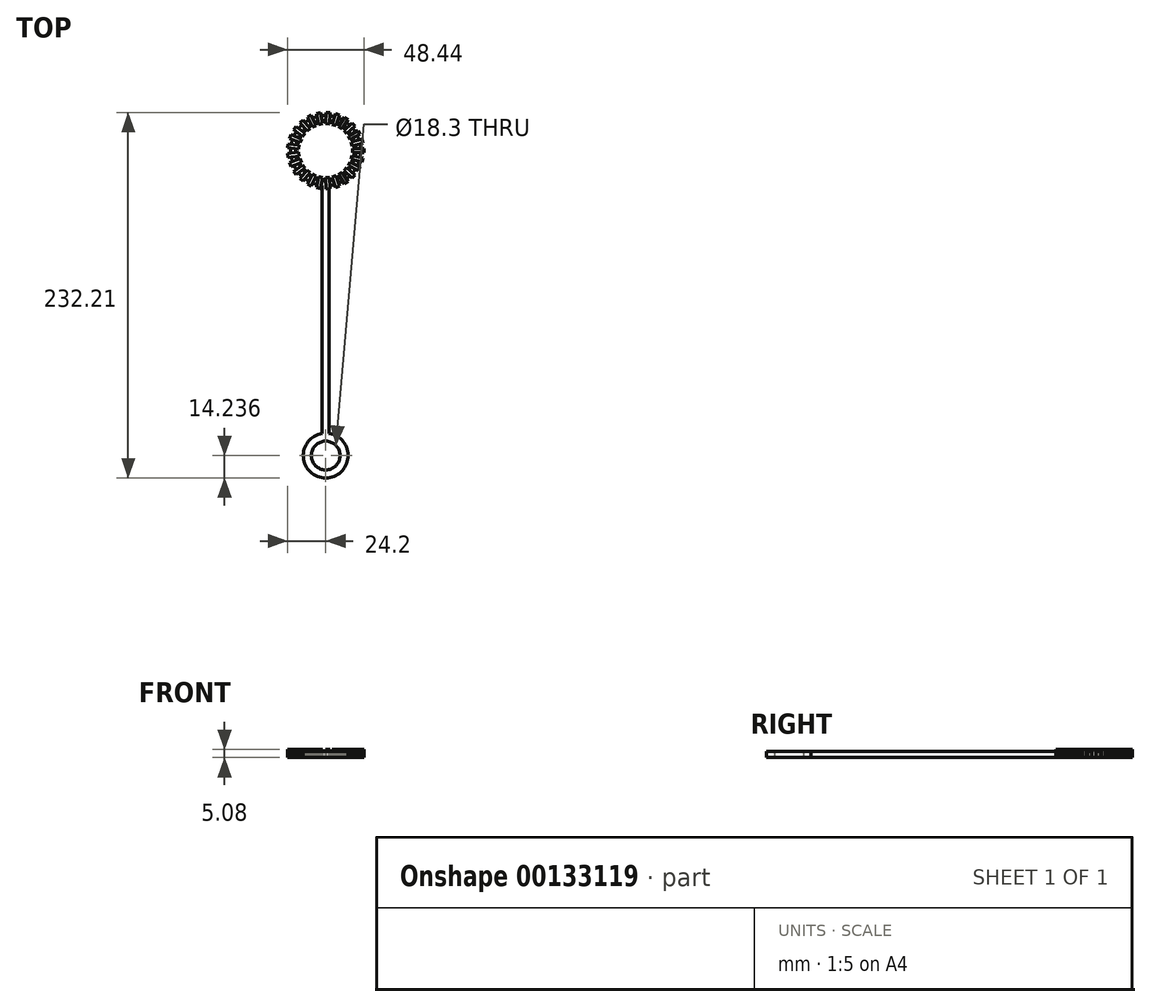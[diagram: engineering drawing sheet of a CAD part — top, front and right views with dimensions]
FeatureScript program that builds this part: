
annotation { "Feature Type Name" : "Feature", "Feature Type Description" : "" }
export const myFeature = defineFeature(function(context is Context, id is Id, definition is map)
    precondition{}
    {
        {
            var Q0;
            Q0=qCreatedBy(makeId("Top.planeOp"),FACE);
            var sketch = newSketch(context, id + "F0", { "sketchPlane" : qUnion([Q0])});
            skCircle(sketch, "E0", {"center": v(0, 0) * mm, "radius": 19.05 * mm});
            skCircle(sketch, "E1", {"center": v(0, 0) * mm, "radius": 22.23 * mm});
            skLineSegment(sketch, "E2", {"start": v(19, 1.27) * mm, "end": v(17.11, 1.27) * mm});
            skLineSegment(sketch, "E3", {"start": v(17.11, 1.27) * mm, "end": v(17.11, 0) * mm});
            skLineSegment(sketch, "E4.MirrorCS", {"start": v(19, -1.27) * mm, "end": v(17.11, -1.27) * mm});
            skLineSegment(sketch, "E5.MirrorCS", {"start": v(17.11, -1.27) * mm, "end": v(17.11, 0) * mm});
            skLineSegment(sketch, "E6.1.0", {"start": v(18.1, 5.96) * mm, "end": v(16.26, 5.49) * mm});
            skLineSegment(sketch, "E6.1.1", {"start": v(18.73, 3.5) * mm, "end": v(16.9, 3.03) * mm});
            skLineSegment(sketch, "E6.1.2", {"start": v(16.9, 3.03) * mm, "end": v(16.58, 4.26) * mm});
            skLineSegment(sketch, "E6.1.3", {"start": v(16.26, 5.49) * mm, "end": v(16.58, 4.26) * mm});
            skLineSegment(sketch, "E6.2.0", {"start": v(16.04, 10.27) * mm, "end": v(14.39, 9.36) * mm});
            skLineSegment(sketch, "E6.2.1", {"start": v(17.27, 8.04) * mm, "end": v(15.6, 7.13) * mm});
            skLineSegment(sketch, "E6.2.2", {"start": v(15.6, 7.13) * mm, "end": v(15, 8.24) * mm});
            skLineSegment(sketch, "E6.2.3", {"start": v(14.39, 9.36) * mm, "end": v(15, 8.24) * mm});
            skLineSegment(sketch, "E6.3.0", {"start": v(12.99, 13.94) * mm, "end": v(11.6, 12.64) * mm});
            skLineSegment(sketch, "E6.3.1", {"start": v(14.73, 12.09) * mm, "end": v(13.35, 10.79) * mm});
            skLineSegment(sketch, "E6.3.2", {"start": v(13.35, 10.79) * mm, "end": v(12.48, 11.72) * mm});
            skLineSegment(sketch, "E6.3.3", {"start": v(11.6, 12.64) * mm, "end": v(12.48, 11.72) * mm});
            skLineSegment(sketch, "E6.4.0", {"start": v(9.11, 16.73) * mm, "end": v(8.1, 15.13) * mm});
            skLineSegment(sketch, "E6.4.1", {"start": v(11.26, 15.37) * mm, "end": v(10.24, 13.77) * mm});
            skLineSegment(sketch, "E6.4.2", {"start": v(10.24, 13.77) * mm, "end": v(9.17, 14.45) * mm});
            skLineSegment(sketch, "E6.4.3", {"start": v(8.1, 15.13) * mm, "end": v(9.17, 14.45) * mm});
            skLineSegment(sketch, "E6.5.0", {"start": v(4.67, 18.47) * mm, "end": v(4.08, 16.67) * mm});
            skLineSegment(sketch, "E6.5.1", {"start": v(7.08, 17.68) * mm, "end": v(6.5, 15.88) * mm});
            skLineSegment(sketch, "E6.5.2", {"start": v(6.5, 15.88) * mm, "end": v(5.29, 16.28) * mm});
            skLineSegment(sketch, "E6.5.3", {"start": v(4.08, 16.67) * mm, "end": v(5.29, 16.28) * mm});
            skLineSegment(sketch, "E6.6.0", {"start": v(-0.07, 19.05) * mm, "end": v(-0.2, 17.16) * mm});
            skLineSegment(sketch, "E6.6.1", {"start": v(2.46, 18.9) * mm, "end": v(2.34, 17) * mm});
            skLineSegment(sketch, "E6.6.2", {"start": v(2.34, 17) * mm, "end": v(1.07, 17.08) * mm});
            skLineSegment(sketch, "E6.6.3", {"start": v(-0.2, 17.16) * mm, "end": v(1.07, 17.08) * mm});
            skLineSegment(sketch, "E6.7.0", {"start": v(-4.8, 18.43) * mm, "end": v(-4.45, 16.57) * mm});
            skLineSegment(sketch, "E6.7.1", {"start": v(-2.31, 18.9) * mm, "end": v(-1.96, 17.05) * mm});
            skLineSegment(sketch, "E6.7.2", {"start": v(-1.96, 17.05) * mm, "end": v(-3.2, 16.81) * mm});
            skLineSegment(sketch, "E6.7.3", {"start": v(-4.45, 16.57) * mm, "end": v(-3.2, 16.81) * mm});
            skLineSegment(sketch, "E6.8.0", {"start": v(-9.24, 16.66) * mm, "end": v(-8.44, 14.94) * mm});
            skLineSegment(sketch, "E6.8.1", {"start": v(-6.94, 17.74) * mm, "end": v(-6.14, 16.03) * mm});
            skLineSegment(sketch, "E6.8.2", {"start": v(-6.14, 16.03) * mm, "end": v(-7.29, 15.49) * mm});
            skLineSegment(sketch, "E6.8.3", {"start": v(-8.44, 14.94) * mm, "end": v(-7.29, 15.49) * mm});
            skLineSegment(sketch, "E6.9.0", {"start": v(-13.1, 13.84) * mm, "end": v(-11.89, 12.38) * mm});
            skLineSegment(sketch, "E6.9.1", {"start": v(-11.14, 15.46) * mm, "end": v(-9.93, 14) * mm});
            skLineSegment(sketch, "E6.9.2", {"start": v(-9.93, 14) * mm, "end": v(-10.9, 13.19) * mm});
            skLineSegment(sketch, "E6.9.3", {"start": v(-11.89, 12.38) * mm, "end": v(-10.9, 13.19) * mm});
            skLineSegment(sketch, "E6.10.0", {"start": v(-16.12, 10.14) * mm, "end": v(-14.6, 9.03) * mm});
            skLineSegment(sketch, "E6.10.1", {"start": v(-14.63, 12.2) * mm, "end": v(-13.1, 11.09) * mm});
            skLineSegment(sketch, "E6.10.2", {"start": v(-13.1, 11.09) * mm, "end": v(-13.85, 10.06) * mm});
            skLineSegment(sketch, "E6.10.3", {"start": v(-14.6, 9.03) * mm, "end": v(-13.85, 10.06) * mm});
            skLineSegment(sketch, "E6.11.0", {"start": v(-18.14, 5.82) * mm, "end": v(-16.38, 5.12) * mm});
            skLineSegment(sketch, "E6.11.1", {"start": v(-17.2, 8.18) * mm, "end": v(-15.45, 7.48) * mm});
            skLineSegment(sketch, "E6.11.2", {"start": v(-15.45, 7.48) * mm, "end": v(-15.91, 6.3) * mm});
            skLineSegment(sketch, "E6.11.3", {"start": v(-16.38, 5.12) * mm, "end": v(-15.91, 6.3) * mm});
            skLineSegment(sketch, "E6.12.0", {"start": v(-19.02, 1.12) * mm, "end": v(-17.14, 0.89) * mm});
            skLineSegment(sketch, "E6.12.1", {"start": v(-18.7, 3.64) * mm, "end": v(-16.82, 3.4) * mm});
            skLineSegment(sketch, "E6.12.2", {"start": v(-16.82, 3.4) * mm, "end": v(-16.98, 2.15) * mm});
            skLineSegment(sketch, "E6.12.3", {"start": v(-17.14, 0.89) * mm, "end": v(-16.98, 2.15) * mm});
            skLineSegment(sketch, "E6.13.0", {"start": v(-18.7, -3.64) * mm, "end": v(-16.82, -3.4) * mm});
            skLineSegment(sketch, "E6.13.1", {"start": v(-19.02, -1.12) * mm, "end": v(-17.14, -0.89) * mm});
            skLineSegment(sketch, "E6.13.2", {"start": v(-17.14, -0.89) * mm, "end": v(-16.98, -2.15) * mm});
            skLineSegment(sketch, "E6.13.3", {"start": v(-16.82, -3.4) * mm, "end": v(-16.98, -2.15) * mm});
            skLineSegment(sketch, "E6.14.0", {"start": v(-17.2, -8.18) * mm, "end": v(-15.45, -7.48) * mm});
            skLineSegment(sketch, "E6.14.1", {"start": v(-18.14, -5.82) * mm, "end": v(-16.38, -5.12) * mm});
            skLineSegment(sketch, "E6.14.2", {"start": v(-16.38, -5.12) * mm, "end": v(-15.91, -6.3) * mm});
            skLineSegment(sketch, "E6.14.3", {"start": v(-15.45, -7.48) * mm, "end": v(-15.91, -6.3) * mm});
            skLineSegment(sketch, "E7.2.15.0", {"start": v(-14.63, -12.2) * mm, "end": v(-13.1, -11.09) * mm});
            skLineSegment(sketch, "E7.3.15.0", {"start": v(-16.12, -10.14) * mm, "end": v(-14.6, -9.03) * mm});
            skLineSegment(sketch, "E7.6.15.0", {"start": v(-14.6, -9.03) * mm, "end": v(-13.85, -10.06) * mm});
            skLineSegment(sketch, "E7.9.15.0", {"start": v(-13.1, -11.09) * mm, "end": v(-13.85, -10.06) * mm});
            skLineSegment(sketch, "E7.2.16.0", {"start": v(-11.14, -15.46) * mm, "end": v(-9.93, -14) * mm});
            skLineSegment(sketch, "E7.3.16.0", {"start": v(-13.1, -13.84) * mm, "end": v(-11.89, -12.38) * mm});
            skLineSegment(sketch, "E7.6.16.0", {"start": v(-11.89, -12.38) * mm, "end": v(-10.9, -13.19) * mm});
            skLineSegment(sketch, "E7.9.16.0", {"start": v(-9.93, -14) * mm, "end": v(-10.9, -13.19) * mm});
            skLineSegment(sketch, "E7.2.17.0", {"start": v(-6.94, -17.74) * mm, "end": v(-6.14, -16.03) * mm});
            skLineSegment(sketch, "E7.3.17.0", {"start": v(-9.24, -16.66) * mm, "end": v(-8.44, -14.94) * mm});
            skLineSegment(sketch, "E7.6.17.0", {"start": v(-8.44, -14.94) * mm, "end": v(-7.29, -15.49) * mm});
            skLineSegment(sketch, "E7.9.17.0", {"start": v(-6.14, -16.03) * mm, "end": v(-7.29, -15.49) * mm});
            skLineSegment(sketch, "E7.2.18.0", {"start": v(-2.31, -18.9) * mm, "end": v(-1.96, -17.05) * mm});
            skLineSegment(sketch, "E7.3.18.0", {"start": v(-4.8, -18.43) * mm, "end": v(-4.45, -16.57) * mm});
            skLineSegment(sketch, "E7.6.18.0", {"start": v(-4.45, -16.57) * mm, "end": v(-3.2, -16.81) * mm});
            skLineSegment(sketch, "E7.9.18.0", {"start": v(-1.96, -17.05) * mm, "end": v(-3.2, -16.81) * mm});
            skLineSegment(sketch, "E7.2.19.0", {"start": v(2.46, -18.9) * mm, "end": v(2.34, -17) * mm});
            skLineSegment(sketch, "E7.3.19.0", {"start": v(-0.07, -19.05) * mm, "end": v(-0.2, -17.16) * mm});
            skLineSegment(sketch, "E7.6.19.0", {"start": v(-0.2, -17.16) * mm, "end": v(1.07, -17.08) * mm});
            skLineSegment(sketch, "E7.9.19.0", {"start": v(2.34, -17) * mm, "end": v(1.07, -17.08) * mm});
            skLineSegment(sketch, "E8.2.20.0", {"start": v(7.08, -17.68) * mm, "end": v(6.5, -15.88) * mm});
            skLineSegment(sketch, "E8.3.20.0", {"start": v(4.67, -18.47) * mm, "end": v(4.08, -16.67) * mm});
            skLineSegment(sketch, "E8.6.20.0", {"start": v(4.08, -16.67) * mm, "end": v(5.29, -16.28) * mm});
            skLineSegment(sketch, "E8.9.20.0", {"start": v(6.5, -15.88) * mm, "end": v(5.29, -16.28) * mm});
            skLineSegment(sketch, "E8.2.21.0", {"start": v(11.26, -15.37) * mm, "end": v(10.24, -13.77) * mm});
            skLineSegment(sketch, "E8.3.21.0", {"start": v(9.11, -16.73) * mm, "end": v(8.1, -15.13) * mm});
            skLineSegment(sketch, "E8.6.21.0", {"start": v(8.1, -15.13) * mm, "end": v(9.17, -14.45) * mm});
            skLineSegment(sketch, "E8.9.21.0", {"start": v(10.24, -13.77) * mm, "end": v(9.17, -14.45) * mm});
            skLineSegment(sketch, "E8.2.22.0", {"start": v(14.73, -12.09) * mm, "end": v(13.35, -10.79) * mm});
            skLineSegment(sketch, "E8.3.22.0", {"start": v(12.99, -13.94) * mm, "end": v(11.6, -12.64) * mm});
            skLineSegment(sketch, "E8.6.22.0", {"start": v(11.6, -12.64) * mm, "end": v(12.48, -11.72) * mm});
            skLineSegment(sketch, "E8.9.22.0", {"start": v(13.35, -10.79) * mm, "end": v(12.48, -11.72) * mm});
            skLineSegment(sketch, "E8.2.23.0", {"start": v(17.27, -8.04) * mm, "end": v(15.6, -7.13) * mm});
            skLineSegment(sketch, "E8.3.23.0", {"start": v(16.04, -10.27) * mm, "end": v(14.39, -9.36) * mm});
            skLineSegment(sketch, "E8.6.23.0", {"start": v(14.39, -9.36) * mm, "end": v(15, -8.24) * mm});
            skLineSegment(sketch, "E8.9.23.0", {"start": v(15.6, -7.13) * mm, "end": v(15, -8.24) * mm});
            skLineSegment(sketch, "E8.2.24.0", {"start": v(18.73, -3.5) * mm, "end": v(16.9, -3.03) * mm});
            skLineSegment(sketch, "E8.3.24.0", {"start": v(18.1, -5.96) * mm, "end": v(16.26, -5.49) * mm});
            skLineSegment(sketch, "E8.6.24.0", {"start": v(16.26, -5.49) * mm, "end": v(16.58, -4.26) * mm});
            skLineSegment(sketch, "E8.9.24.0", {"start": v(16.9, -3.03) * mm, "end": v(16.58, -4.26) * mm});
            skSolve(sketch);
        }
        {
            var Q0;
            Q0=makeQuery(id+"F0.imprint","IMPRINT",FACE,{"disambiguationData":[TD([[makeQuery(id+"F0.imprint","IMPRINT",EDGE,{"derivedFrom":sQuery(id+"F0.wireOp",EDGE,"E1")}),1.0]])]});
            var Q1;
            {var subQ1=sQuery(id+"F0.wireOp",EDGE,"E6.5.0");Q1=makeQuery(id+"F0.imprint","IMPRINT",FACE,{"disambiguationData":[TD([[makeQuery(id+"F0.imprint","IMPRINT",EDGE,{"derivedFrom":subQ1}),1.0]])]});}
            var Q2;
            {var subQ1=sQuery(id+"F0.wireOp",EDGE,"E6.6.0");Q2=makeQuery(id+"F0.imprint","IMPRINT",FACE,{"disambiguationData":[TD([[makeQuery(id+"F0.imprint","IMPRINT",EDGE,{"derivedFrom":subQ1}),1.0]])]});}
            var Q3;
            {var subQ1=sQuery(id+"F0.wireOp",EDGE,"E6.7.0");Q3=makeQuery(id+"F0.imprint","IMPRINT",FACE,{"disambiguationData":[TD([[makeQuery(id+"F0.imprint","IMPRINT",EDGE,{"derivedFrom":subQ1}),1.0]])]});}
            var Q4;
            {var subQ1=sQuery(id+"F0.wireOp",EDGE,"E6.8.0");Q4=makeQuery(id+"F0.imprint","IMPRINT",FACE,{"disambiguationData":[TD([[makeQuery(id+"F0.imprint","IMPRINT",EDGE,{"derivedFrom":subQ1}),1.0]])]});}
            var Q5;
            {var subQ1=sQuery(id+"F0.wireOp",EDGE,"E6.10.0");Q5=makeQuery(id+"F0.imprint","IMPRINT",FACE,{"disambiguationData":[TD([[makeQuery(id+"F0.imprint","IMPRINT",EDGE,{"derivedFrom":subQ1}),1.0]])]});}
            var Q6;
            {var subQ1=sQuery(id+"F0.wireOp",EDGE,"E6.11.0");Q6=makeQuery(id+"F0.imprint","IMPRINT",FACE,{"disambiguationData":[TD([[makeQuery(id+"F0.imprint","IMPRINT",EDGE,{"derivedFrom":subQ1}),1.0]])]});}
            var Q7;
            {var subQ1=sQuery(id+"F0.wireOp",EDGE,"E6.9.0");Q7=makeQuery(id+"F0.imprint","IMPRINT",FACE,{"disambiguationData":[TD([[makeQuery(id+"F0.imprint","IMPRINT",EDGE,{"derivedFrom":subQ1}),1.0]])]});}
            var Q8;
            {var subQ1=sQuery(id+"F0.wireOp",EDGE,"E6.4.0");Q8=makeQuery(id+"F0.imprint","IMPRINT",FACE,{"disambiguationData":[TD([[makeQuery(id+"F0.imprint","IMPRINT",EDGE,{"derivedFrom":subQ1}),1.0]])]});}
            var Q9;
            {var subQ1=sQuery(id+"F0.wireOp",EDGE,"E6.3.0");Q9=makeQuery(id+"F0.imprint","IMPRINT",FACE,{"disambiguationData":[TD([[makeQuery(id+"F0.imprint","IMPRINT",EDGE,{"derivedFrom":subQ1}),1.0]])]});}
            var Q10;
            {var subQ1=sQuery(id+"F0.wireOp",EDGE,"E6.2.0");Q10=makeQuery(id+"F0.imprint","IMPRINT",FACE,{"disambiguationData":[TD([[makeQuery(id+"F0.imprint","IMPRINT",EDGE,{"derivedFrom":subQ1}),1.0]])]});}
            var Q11;
            {var subQ1=sQuery(id+"F0.wireOp",EDGE,"E6.1.0");Q11=makeQuery(id+"F0.imprint","IMPRINT",FACE,{"disambiguationData":[TD([[makeQuery(id+"F0.imprint","IMPRINT",EDGE,{"derivedFrom":subQ1}),1.0]])]});}
            var Q12;
            {var subQ1=sQuery(id+"F0.wireOp",EDGE,"E2");Q12=makeQuery(id+"F0.imprint","IMPRINT",FACE,{"disambiguationData":[TD([[makeQuery(id+"F0.imprint","IMPRINT",EDGE,{"derivedFrom":subQ1}),1.0]])]});}
            var Q13;
            {var subQ1=sQuery(id+"F0.wireOp",EDGE,"E7.2.19.0");Q13=makeQuery(id+"F0.imprint","IMPRINT",FACE,{"disambiguationData":[TD([[makeQuery(id+"F0.imprint","IMPRINT",EDGE,{"derivedFrom":subQ1}),1.0]])]});}
            var Q14;
            {var subQ1=sQuery(id+"F0.wireOp",EDGE,"E7.2.18.0");Q14=makeQuery(id+"F0.imprint","IMPRINT",FACE,{"disambiguationData":[TD([[makeQuery(id+"F0.imprint","IMPRINT",EDGE,{"derivedFrom":subQ1}),1.0]])]});}
            var Q15;
            {var subQ1=sQuery(id+"F0.wireOp",EDGE,"E7.2.17.0");Q15=makeQuery(id+"F0.imprint","IMPRINT",FACE,{"disambiguationData":[TD([[makeQuery(id+"F0.imprint","IMPRINT",EDGE,{"derivedFrom":subQ1}),1.0]])]});}
            var Q16;
            {var subQ0=sQuery(id+"F0.wireOp",EDGE,"E7.2.16.0");Q16=makeQuery(id+"F0.imprint","IMPRINT",FACE,{"disambiguationData":[TD([[makeQuery(id+"F0.imprint","IMPRINT",EDGE,{"derivedFrom":subQ0}),1.0]])]});}
            var Q17;
            {var subQ1=sQuery(id+"F0.wireOp",EDGE,"E7.2.15.0");Q17=makeQuery(id+"F0.imprint","IMPRINT",FACE,{"disambiguationData":[TD([[makeQuery(id+"F0.imprint","IMPRINT",EDGE,{"derivedFrom":subQ1}),1.0]])]});}
            var Q18;
            {var subQ1=sQuery(id+"F0.wireOp",EDGE,"E6.14.0");Q18=makeQuery(id+"F0.imprint","IMPRINT",FACE,{"disambiguationData":[TD([[makeQuery(id+"F0.imprint","IMPRINT",EDGE,{"derivedFrom":subQ1}),1.0]])]});}
            var Q19;
            {var subQ1=sQuery(id+"F0.wireOp",EDGE,"E6.13.0");Q19=makeQuery(id+"F0.imprint","IMPRINT",FACE,{"disambiguationData":[TD([[makeQuery(id+"F0.imprint","IMPRINT",EDGE,{"derivedFrom":subQ1}),1.0]])]});}
            var Q20;
            {var subQ1=sQuery(id+"F0.wireOp",EDGE,"E6.12.0");Q20=makeQuery(id+"F0.imprint","IMPRINT",FACE,{"disambiguationData":[TD([[makeQuery(id+"F0.imprint","IMPRINT",EDGE,{"derivedFrom":subQ1}),1.0]])]});}
            extrude(context, id + "F1", {"entities" : qUnion([Q0, Q1, Q2, Q3, Q4, Q5, Q6, Q7, Q8, Q9, Q10, Q11, Q12, Q13, Q14, Q15, Q16, Q17, Q18, Q19, Q20]), "depth" : 3.8 * mm});
        }
        {
            var Q0;
            Q0=makeQuery(id+"F1.opExtrude","CAP_FACE",FACE,{"disambiguationData":[OSD([sQuery(id+"F0.wireOp",EDGE,"E0"),sQuery(id+"F0.wireOp",EDGE,"E1"),sQuery(id+"F0.wireOp",EDGE,"E2"),sQuery(id+"F0.wireOp",EDGE,"E3"),sQuery(id+"F0.wireOp",EDGE,"E4.MirrorCS"),sQuery(id+"F0.wireOp",EDGE,"E5.MirrorCS"),sQuery(id+"F0.wireOp",EDGE,"E6.1.0"),sQuery(id+"F0.wireOp",EDGE,"E6.1.1"),sQuery(id+"F0.wireOp",EDGE,"E6.1.2"),sQuery(id+"F0.wireOp",EDGE,"E6.1.3"),sQuery(id+"F0.wireOp",EDGE,"E6.2.0"),sQuery(id+"F0.wireOp",EDGE,"E6.2.1"),sQuery(id+"F0.wireOp",EDGE,"E6.2.2"),sQuery(id+"F0.wireOp",EDGE,"E6.2.3"),sQuery(id+"F0.wireOp",EDGE,"E6.3.0"),sQuery(id+"F0.wireOp",EDGE,"E6.3.1"),sQuery(id+"F0.wireOp",EDGE,"E6.3.2"),sQuery(id+"F0.wireOp",EDGE,"E6.3.3"),sQuery(id+"F0.wireOp",EDGE,"E6.4.0"),sQuery(id+"F0.wireOp",EDGE,"E6.4.1"),sQuery(id+"F0.wireOp",EDGE,"E6.4.2"),sQuery(id+"F0.wireOp",EDGE,"E6.4.3"),sQuery(id+"F0.wireOp",EDGE,"E6.5.0"),sQuery(id+"F0.wireOp",EDGE,"E6.5.1"),sQuery(id+"F0.wireOp",EDGE,"E6.5.2"),sQuery(id+"F0.wireOp",EDGE,"E6.5.3"),sQuery(id+"F0.wireOp",EDGE,"E6.6.0"),sQuery(id+"F0.wireOp",EDGE,"E6.6.1"),sQuery(id+"F0.wireOp",EDGE,"E6.6.2"),sQuery(id+"F0.wireOp",EDGE,"E6.6.3"),sQuery(id+"F0.wireOp",EDGE,"E6.7.0"),sQuery(id+"F0.wireOp",EDGE,"E6.7.1"),sQuery(id+"F0.wireOp",EDGE,"E6.7.2"),sQuery(id+"F0.wireOp",EDGE,"E6.7.3"),sQuery(id+"F0.wireOp",EDGE,"E6.8.0"),sQuery(id+"F0.wireOp",EDGE,"E6.8.1"),sQuery(id+"F0.wireOp",EDGE,"E6.8.2"),sQuery(id+"F0.wireOp",EDGE,"E6.8.3"),sQuery(id+"F0.wireOp",EDGE,"E6.9.0"),sQuery(id+"F0.wireOp",EDGE,"E6.9.1"),sQuery(id+"F0.wireOp",EDGE,"E6.9.2"),sQuery(id+"F0.wireOp",EDGE,"E6.9.3"),sQuery(id+"F0.wireOp",EDGE,"E6.10.0"),sQuery(id+"F0.wireOp",EDGE,"E6.10.1"),sQuery(id+"F0.wireOp",EDGE,"E6.10.2"),sQuery(id+"F0.wireOp",EDGE,"E6.10.3"),sQuery(id+"F0.wireOp",EDGE,"E6.11.0"),sQuery(id+"F0.wireOp",EDGE,"E6.11.1"),sQuery(id+"F0.wireOp",EDGE,"E6.11.2"),sQuery(id+"F0.wireOp",EDGE,"E6.11.3"),sQuery(id+"F0.wireOp",EDGE,"E6.12.0"),sQuery(id+"F0.wireOp",EDGE,"E6.12.1"),sQuery(id+"F0.wireOp",EDGE,"E6.12.2"),sQuery(id+"F0.wireOp",EDGE,"E6.12.3"),sQuery(id+"F0.wireOp",EDGE,"E6.13.0"),sQuery(id+"F0.wireOp",EDGE,"E6.13.1"),sQuery(id+"F0.wireOp",EDGE,"E6.13.2"),sQuery(id+"F0.wireOp",EDGE,"E6.13.3"),sQuery(id+"F0.wireOp",EDGE,"E6.14.0"),sQuery(id+"F0.wireOp",EDGE,"E6.14.1"),sQuery(id+"F0.wireOp",EDGE,"E6.14.2"),sQuery(id+"F0.wireOp",EDGE,"E6.14.3"),sQuery(id+"F0.wireOp",EDGE,"E7.2.15.0"),sQuery(id+"F0.wireOp",EDGE,"E7.3.15.0"),sQuery(id+"F0.wireOp",EDGE,"E7.6.15.0"),sQuery(id+"F0.wireOp",EDGE,"E7.9.15.0"),sQuery(id+"F0.wireOp",EDGE,"E7.2.16.0"),sQuery(id+"F0.wireOp",EDGE,"E7.3.16.0"),sQuery(id+"F0.wireOp",EDGE,"E7.6.16.0"),sQuery(id+"F0.wireOp",EDGE,"E7.9.16.0"),sQuery(id+"F0.wireOp",EDGE,"E7.2.17.0"),sQuery(id+"F0.wireOp",EDGE,"E7.3.17.0"),sQuery(id+"F0.wireOp",EDGE,"E7.6.17.0"),sQuery(id+"F0.wireOp",EDGE,"E7.9.17.0"),sQuery(id+"F0.wireOp",EDGE,"E7.2.18.0"),sQuery(id+"F0.wireOp",EDGE,"E7.3.18.0"),sQuery(id+"F0.wireOp",EDGE,"E7.6.18.0"),sQuery(id+"F0.wireOp",EDGE,"E7.9.18.0"),sQuery(id+"F0.wireOp",EDGE,"E7.2.19.0"),sQuery(id+"F0.wireOp",EDGE,"E7.3.19.0"),sQuery(id+"F0.wireOp",EDGE,"E7.6.19.0"),sQuery(id+"F0.wireOp",EDGE,"E7.9.19.0")])],"isStart":false});
            var sketch = newSketch(context, id + "F2", { "sketchPlane" : qUnion([Q0])});
            skLineSegment(sketch, "E9.bottom", {"start": v(17.11, 1.27) * mm, "end": v(22.19, 1.27) * mm});
            skLineSegment(sketch, "E9.top", {"start": v(17.11, -1.27) * mm, "end": v(22.19, -1.27) * mm});
            skLineSegment(sketch, "E9.left", {"start": v(17.11, 1.27) * mm, "end": v(17.11, -1.27) * mm});
            skLineSegment(sketch, "E10.1.0", {"start": v(16.26, 5.49) * mm, "end": v(21.18, 6.75) * mm});
            skLineSegment(sketch, "E10.1.1", {"start": v(16.26, 5.49) * mm, "end": v(16.9, 3.03) * mm});
            skLineSegment(sketch, "E10.1.2", {"start": v(16.9, 3.03) * mm, "end": v(21.8, 4.3) * mm});
            skLineSegment(sketch, "E10.1.3", {"start": v(21.18, 6.75) * mm, "end": v(21.8, 4.3) * mm});
            skLineSegment(sketch, "E10.2.0", {"start": v(14.39, 9.36) * mm, "end": v(18.83, 11.8) * mm});
            skLineSegment(sketch, "E10.2.1", {"start": v(14.39, 9.36) * mm, "end": v(15.6, 7.13) * mm});
            skLineSegment(sketch, "E10.2.2", {"start": v(15.6, 7.13) * mm, "end": v(20.05, 9.58) * mm});
            skLineSegment(sketch, "E10.2.3", {"start": v(18.83, 11.8) * mm, "end": v(20.05, 9.58) * mm});
            skLineSegment(sketch, "E10.3.0", {"start": v(11.6, 12.64) * mm, "end": v(15.3, 16.12) * mm});
            skLineSegment(sketch, "E10.3.1", {"start": v(11.6, 12.64) * mm, "end": v(13.34, 10.8) * mm});
            skLineSegment(sketch, "E10.3.2", {"start": v(13.34, 10.8) * mm, "end": v(17.04, 14.27) * mm});
            skLineSegment(sketch, "E10.3.3", {"start": v(15.3, 16.12) * mm, "end": v(17.04, 14.27) * mm});
            skLineSegment(sketch, "E10.4.0", {"start": v(8.1, 15.13) * mm, "end": v(10.82, 19.42) * mm});
            skLineSegment(sketch, "E10.4.1", {"start": v(8.1, 15.13) * mm, "end": v(10.24, 13.77) * mm});
            skLineSegment(sketch, "E10.4.2", {"start": v(10.24, 13.77) * mm, "end": v(12.96, 18.06) * mm});
            skLineSegment(sketch, "E10.4.3", {"start": v(10.82, 19.42) * mm, "end": v(12.96, 18.06) * mm});
            skLineSegment(sketch, "E10.5.0", {"start": v(4.08, 16.67) * mm, "end": v(5.65, 21.5) * mm});
            skLineSegment(sketch, "E10.5.1", {"start": v(4.08, 16.67) * mm, "end": v(6.5, 15.89) * mm});
            skLineSegment(sketch, "E10.5.2", {"start": v(6.5, 15.89) * mm, "end": v(8.06, 20.71) * mm});
            skLineSegment(sketch, "E10.5.3", {"start": v(5.65, 21.5) * mm, "end": v(8.06, 20.71) * mm});
            skLineSegment(sketch, "E10.6.0", {"start": v(-0.2, 17.16) * mm, "end": v(0.13, 22.22) * mm});
            skLineSegment(sketch, "E10.6.1", {"start": v(-0.2, 17.16) * mm, "end": v(2.34, 17) * mm});
            skLineSegment(sketch, "E10.6.2", {"start": v(2.34, 17) * mm, "end": v(2.66, 22.07) * mm});
            skLineSegment(sketch, "E10.6.3", {"start": v(0.13, 22.22) * mm, "end": v(2.66, 22.07) * mm});
            skLineSegment(sketch, "E10.7.0", {"start": v(-4.45, 16.57) * mm, "end": v(-5.4, 21.56) * mm});
            skLineSegment(sketch, "E10.7.1", {"start": v(-4.45, 16.57) * mm, "end": v(-1.96, 17.05) * mm});
            skLineSegment(sketch, "E10.7.2", {"start": v(-1.96, 17.05) * mm, "end": v(-2.91, 22.03) * mm});
            skLineSegment(sketch, "E10.7.3", {"start": v(-5.4, 21.56) * mm, "end": v(-2.91, 22.03) * mm});
            skLineSegment(sketch, "E10.8.0", {"start": v(-8.44, 14.94) * mm, "end": v(-10.6, 19.54) * mm});
            skLineSegment(sketch, "E10.8.1", {"start": v(-8.44, 14.94) * mm, "end": v(-6.14, 16.03) * mm});
            skLineSegment(sketch, "E10.8.2", {"start": v(-6.14, 16.03) * mm, "end": v(-8.3, 20.62) * mm});
            skLineSegment(sketch, "E10.8.3", {"start": v(-10.6, 19.54) * mm, "end": v(-8.3, 20.62) * mm});
            skLineSegment(sketch, "E10.9.0", {"start": v(-11.89, 12.38) * mm, "end": v(-15.12, 16.29) * mm});
            skLineSegment(sketch, "E10.9.1", {"start": v(-11.89, 12.38) * mm, "end": v(-9.93, 14) * mm});
            skLineSegment(sketch, "E10.9.2", {"start": v(-9.93, 14) * mm, "end": v(-13.17, 17.9) * mm});
            skLineSegment(sketch, "E10.9.3", {"start": v(-15.12, 16.29) * mm, "end": v(-13.17, 17.9) * mm});
            skLineSegment(sketch, "E10.10.0", {"start": v(-14.6, 9.03) * mm, "end": v(-18.7, 12.01) * mm});
            skLineSegment(sketch, "E10.10.1", {"start": v(-14.6, 9.03) * mm, "end": v(-13.1, 11.09) * mm});
            skLineSegment(sketch, "E10.10.2", {"start": v(-13.1, 11.09) * mm, "end": v(-17.2, 14.07) * mm});
            skLineSegment(sketch, "E10.10.3", {"start": v(-18.7, 12.01) * mm, "end": v(-17.2, 14.07) * mm});
            skLineSegment(sketch, "E10.11.0", {"start": v(-16.38, 5.12) * mm, "end": v(-21.1, 6.99) * mm});
            skLineSegment(sketch, "E10.11.1", {"start": v(-16.38, 5.12) * mm, "end": v(-15.45, 7.48) * mm});
            skLineSegment(sketch, "E10.11.2", {"start": v(-15.45, 7.48) * mm, "end": v(-20.16, 9.35) * mm});
            skLineSegment(sketch, "E10.11.3", {"start": v(-21.1, 6.99) * mm, "end": v(-20.16, 9.35) * mm});
            skLineSegment(sketch, "E10.12.0", {"start": v(-17.14, 0.89) * mm, "end": v(-22.17, 1.52) * mm});
            skLineSegment(sketch, "E10.12.1", {"start": v(-17.14, 0.89) * mm, "end": v(-16.82, 3.4) * mm});
            skLineSegment(sketch, "E10.12.2", {"start": v(-16.82, 3.4) * mm, "end": v(-21.85, 4.04) * mm});
            skLineSegment(sketch, "E10.12.3", {"start": v(-22.17, 1.52) * mm, "end": v(-21.85, 4.04) * mm});
            skLineSegment(sketch, "E10.13.0", {"start": v(-16.82, -3.4) * mm, "end": v(-21.85, -4.04) * mm});
            skLineSegment(sketch, "E10.13.1", {"start": v(-16.82, -3.4) * mm, "end": v(-17.14, -0.89) * mm});
            skLineSegment(sketch, "E10.13.2", {"start": v(-17.14, -0.89) * mm, "end": v(-22.17, -1.52) * mm});
            skLineSegment(sketch, "E10.13.3", {"start": v(-21.85, -4.04) * mm, "end": v(-22.17, -1.52) * mm});
            skLineSegment(sketch, "E10.14.0", {"start": v(-15.45, -7.48) * mm, "end": v(-20.16, -9.35) * mm});
            skLineSegment(sketch, "E10.14.1", {"start": v(-15.45, -7.48) * mm, "end": v(-16.38, -5.12) * mm});
            skLineSegment(sketch, "E10.14.2", {"start": v(-16.38, -5.12) * mm, "end": v(-21.1, -6.99) * mm});
            skLineSegment(sketch, "E10.14.3", {"start": v(-20.16, -9.35) * mm, "end": v(-21.1, -6.99) * mm});
            skLineSegment(sketch, "E10.15.0", {"start": v(-13.1, -11.09) * mm, "end": v(-17.2, -14.07) * mm});
            skLineSegment(sketch, "E10.15.1", {"start": v(-13.1, -11.09) * mm, "end": v(-14.6, -9.03) * mm});
            skLineSegment(sketch, "E10.15.2", {"start": v(-14.6, -9.03) * mm, "end": v(-18.7, -12.02) * mm});
            skLineSegment(sketch, "E10.15.3", {"start": v(-17.2, -14.07) * mm, "end": v(-18.7, -12.02) * mm});
            skLineSegment(sketch, "E10.16.0", {"start": v(-9.93, -14) * mm, "end": v(-13.17, -17.9) * mm});
            skLineSegment(sketch, "E10.16.1", {"start": v(-9.93, -14) * mm, "end": v(-11.89, -12.38) * mm});
            skLineSegment(sketch, "E10.16.2", {"start": v(-11.89, -12.38) * mm, "end": v(-15.12, -16.29) * mm});
            skLineSegment(sketch, "E10.16.3", {"start": v(-13.17, -17.9) * mm, "end": v(-15.12, -16.29) * mm});
            skLineSegment(sketch, "E10.17.0", {"start": v(-6.14, -16.03) * mm, "end": v(-8.3, -20.62) * mm});
            skLineSegment(sketch, "E10.17.1", {"start": v(-6.14, -16.03) * mm, "end": v(-8.43, -14.95) * mm});
            skLineSegment(sketch, "E10.17.2", {"start": v(-8.43, -14.95) * mm, "end": v(-10.6, -19.54) * mm});
            skLineSegment(sketch, "E10.17.3", {"start": v(-8.3, -20.62) * mm, "end": v(-10.6, -19.54) * mm});
            skLineSegment(sketch, "E10.18.0", {"start": v(-1.96, -17.05) * mm, "end": v(-2.91, -22.03) * mm});
            skLineSegment(sketch, "E10.18.1", {"start": v(-1.96, -17.05) * mm, "end": v(-4.45, -16.57) * mm});
            skLineSegment(sketch, "E10.18.2", {"start": v(-4.45, -16.57) * mm, "end": v(-5.4, -21.56) * mm});
            skLineSegment(sketch, "E10.18.3", {"start": v(-2.91, -22.03) * mm, "end": v(-5.4, -21.56) * mm});
            skLineSegment(sketch, "E10.19.0", {"start": v(2.34, -17) * mm, "end": v(2.66, -22.07) * mm});
            skLineSegment(sketch, "E10.19.1", {"start": v(2.34, -17) * mm, "end": v(-0.2, -17.16) * mm});
            skLineSegment(sketch, "E10.19.2", {"start": v(-0.2, -17.16) * mm, "end": v(0.13, -22.22) * mm});
            skLineSegment(sketch, "E10.19.3", {"start": v(2.66, -22.07) * mm, "end": v(0.13, -22.22) * mm});
            skPoint(sketch, "E10.center", {"position": v(0, 0) * mm});
            skLineSegment(sketch, "E11.bottom", {"start": v(22.19, 1.27) * mm, "end": v(24.24, 1.27) * mm});
            skLineSegment(sketch, "E11.top", {"start": v(22.19, -1.27) * mm, "end": v(24.24, -1.27) * mm});
            skLineSegment(sketch, "E11.right", {"start": v(24.24, 1.27) * mm, "end": v(24.24, -1.27) * mm});
            skLineSegment(sketch, "E12.1.0", {"start": v(21.8, 4.3) * mm, "end": v(23.79, 4.8) * mm});
            skLineSegment(sketch, "E12.1.1", {"start": v(23.16, 7.26) * mm, "end": v(23.79, 4.8) * mm});
            skLineSegment(sketch, "E12.1.2", {"start": v(21.18, 6.75) * mm, "end": v(23.16, 7.26) * mm});
            skLineSegment(sketch, "E12.2.0", {"start": v(20.05, 9.58) * mm, "end": v(21.85, 10.56) * mm});
            skLineSegment(sketch, "E12.2.1", {"start": v(20.63, 12.79) * mm, "end": v(21.85, 10.56) * mm});
            skLineSegment(sketch, "E12.2.2", {"start": v(18.83, 11.8) * mm, "end": v(20.63, 12.79) * mm});
            skLineSegment(sketch, "E12.3.0", {"start": v(17.04, 14.27) * mm, "end": v(18.53, 15.67) * mm});
            skLineSegment(sketch, "E12.3.1", {"start": v(16.8, 17.52) * mm, "end": v(18.53, 15.67) * mm});
            skLineSegment(sketch, "E12.3.2", {"start": v(15.3, 16.12) * mm, "end": v(16.8, 17.52) * mm});
            skLineSegment(sketch, "E12.4.0", {"start": v(12.96, 18.06) * mm, "end": v(14.06, 19.78) * mm});
            skLineSegment(sketch, "E12.4.1", {"start": v(11.91, 21.14) * mm, "end": v(14.06, 19.78) * mm});
            skLineSegment(sketch, "E12.4.2", {"start": v(10.82, 19.42) * mm, "end": v(11.91, 21.14) * mm});
            skLineSegment(sketch, "E12.5.0", {"start": v(8.06, 20.71) * mm, "end": v(8.7, 22.66) * mm});
            skLineSegment(sketch, "E12.5.1", {"start": v(6.28, 23.44) * mm, "end": v(8.7, 22.66) * mm});
            skLineSegment(sketch, "E12.5.2", {"start": v(5.65, 21.5) * mm, "end": v(6.28, 23.44) * mm});
            skLineSegment(sketch, "E12.6.0", {"start": v(2.66, 22.07) * mm, "end": v(2.79, 24.1) * mm});
            skLineSegment(sketch, "E12.6.1", {"start": v(0.25, 24.27) * mm, "end": v(2.79, 24.1) * mm});
            skLineSegment(sketch, "E12.6.2", {"start": v(0.13, 22.22) * mm, "end": v(0.25, 24.27) * mm});
            skLineSegment(sketch, "E12.7.0", {"start": v(-2.91, 22.03) * mm, "end": v(-3.3, 24.04) * mm});
            skLineSegment(sketch, "E12.7.1", {"start": v(-5.79, 23.57) * mm, "end": v(-3.3, 24.04) * mm});
            skLineSegment(sketch, "E12.7.2", {"start": v(-5.4, 21.56) * mm, "end": v(-5.79, 23.57) * mm});
            skLineSegment(sketch, "E12.8.0", {"start": v(-8.3, 20.62) * mm, "end": v(-9.17, 22.47) * mm});
            skLineSegment(sketch, "E12.8.1", {"start": v(-11.47, 21.39) * mm, "end": v(-9.17, 22.47) * mm});
            skLineSegment(sketch, "E12.8.2", {"start": v(-10.6, 19.54) * mm, "end": v(-11.47, 21.39) * mm});
            skLineSegment(sketch, "E12.9.0", {"start": v(-13.17, 17.9) * mm, "end": v(-14.47, 19.48) * mm});
            skLineSegment(sketch, "E12.9.1", {"start": v(-16.43, 17.86) * mm, "end": v(-14.47, 19.48) * mm});
            skLineSegment(sketch, "E12.9.2", {"start": v(-15.12, 16.29) * mm, "end": v(-16.43, 17.86) * mm});
            skLineSegment(sketch, "E12.10.0", {"start": v(-17.2, 14.07) * mm, "end": v(-18.86, 15.27) * mm});
            skLineSegment(sketch, "E12.10.1", {"start": v(-20.35, 13.22) * mm, "end": v(-18.86, 15.27) * mm});
            skLineSegment(sketch, "E12.10.2", {"start": v(-18.7, 12.01) * mm, "end": v(-20.35, 13.22) * mm});
            skLineSegment(sketch, "E12.11.0", {"start": v(-20.16, 9.35) * mm, "end": v(-22.07, 10.1) * mm});
            skLineSegment(sketch, "E12.11.1", {"start": v(-23, 7.74) * mm, "end": v(-22.07, 10.1) * mm});
            skLineSegment(sketch, "E12.11.2", {"start": v(-21.1, 6.99) * mm, "end": v(-23, 7.74) * mm});
            skLineSegment(sketch, "E12.12.0", {"start": v(-21.85, 4.04) * mm, "end": v(-23.89, 4.3) * mm});
            skLineSegment(sketch, "E12.12.1", {"start": v(-24.2, 1.78) * mm, "end": v(-23.89, 4.3) * mm});
            skLineSegment(sketch, "E12.12.2", {"start": v(-22.17, 1.52) * mm, "end": v(-24.2, 1.78) * mm});
            skLineSegment(sketch, "E12.13.0", {"start": v(-22.17, -1.52) * mm, "end": v(-24.2, -1.78) * mm});
            skLineSegment(sketch, "E12.13.1", {"start": v(-23.89, -4.3) * mm, "end": v(-24.2, -1.78) * mm});
            skLineSegment(sketch, "E12.13.2", {"start": v(-21.85, -4.04) * mm, "end": v(-23.89, -4.3) * mm});
            skLineSegment(sketch, "E12.14.0", {"start": v(-21.1, -6.99) * mm, "end": v(-23, -7.74) * mm});
            skLineSegment(sketch, "E12.14.1", {"start": v(-22.07, -10.1) * mm, "end": v(-23, -7.74) * mm});
            skLineSegment(sketch, "E12.14.2", {"start": v(-20.16, -9.35) * mm, "end": v(-22.07, -10.1) * mm});
            skLineSegment(sketch, "E12.15.0", {"start": v(-18.7, -12.02) * mm, "end": v(-20.35, -13.22) * mm});
            skLineSegment(sketch, "E12.15.1", {"start": v(-18.86, -15.27) * mm, "end": v(-20.35, -13.22) * mm});
            skLineSegment(sketch, "E12.15.2", {"start": v(-17.2, -14.07) * mm, "end": v(-18.86, -15.27) * mm});
            skLineSegment(sketch, "E12.16.0", {"start": v(-15.12, -16.29) * mm, "end": v(-16.43, -17.87) * mm});
            skLineSegment(sketch, "E12.16.1", {"start": v(-14.47, -19.48) * mm, "end": v(-16.43, -17.87) * mm});
            skLineSegment(sketch, "E12.16.2", {"start": v(-13.17, -17.9) * mm, "end": v(-14.47, -19.48) * mm});
            skLineSegment(sketch, "E12.17.0", {"start": v(-10.6, -19.54) * mm, "end": v(-11.47, -21.39) * mm});
            skLineSegment(sketch, "E12.17.1", {"start": v(-9.17, -22.47) * mm, "end": v(-11.47, -21.39) * mm});
            skLineSegment(sketch, "E12.17.2", {"start": v(-8.3, -20.62) * mm, "end": v(-9.17, -22.47) * mm});
            skLineSegment(sketch, "E12.18.0", {"start": v(-5.4, -21.56) * mm, "end": v(-5.79, -23.57) * mm});
            skLineSegment(sketch, "E12.18.1", {"start": v(-3.3, -24.04) * mm, "end": v(-5.79, -23.57) * mm});
            skLineSegment(sketch, "E12.18.2", {"start": v(-2.91, -22.03) * mm, "end": v(-3.3, -24.04) * mm});
            skLineSegment(sketch, "E12.19.0", {"start": v(0.13, -22.22) * mm, "end": v(0.26, -24.27) * mm});
            skLineSegment(sketch, "E12.19.1", {"start": v(2.79, -24.1) * mm, "end": v(0.26, -24.27) * mm});
            skLineSegment(sketch, "E12.19.2", {"start": v(2.66, -22.07) * mm, "end": v(2.79, -24.1) * mm});
            skLineSegment(sketch, "E13.1.20.0", {"start": v(6.5, -15.88) * mm, "end": v(8.06, -20.71) * mm});
            skLineSegment(sketch, "E13.3.20.0", {"start": v(6.5, -15.88) * mm, "end": v(4.08, -16.67) * mm});
            skLineSegment(sketch, "E13.6.20.0", {"start": v(4.08, -16.67) * mm, "end": v(5.65, -21.5) * mm});
            skLineSegment(sketch, "E13.9.20.0", {"start": v(8.06, -20.71) * mm, "end": v(5.65, -21.5) * mm});
            skLineSegment(sketch, "E13.1.21.0", {"start": v(10.24, -13.77) * mm, "end": v(12.96, -18.05) * mm});
            skLineSegment(sketch, "E13.3.21.0", {"start": v(10.24, -13.77) * mm, "end": v(8.1, -15.13) * mm});
            skLineSegment(sketch, "E13.6.21.0", {"start": v(8.1, -15.13) * mm, "end": v(10.82, -19.41) * mm});
            skLineSegment(sketch, "E13.9.21.0", {"start": v(12.96, -18.05) * mm, "end": v(10.82, -19.41) * mm});
            skLineSegment(sketch, "E13.1.22.0", {"start": v(13.35, -10.79) * mm, "end": v(17.04, -14.26) * mm});
            skLineSegment(sketch, "E13.3.22.0", {"start": v(13.35, -10.79) * mm, "end": v(11.6, -12.64) * mm});
            skLineSegment(sketch, "E13.6.22.0", {"start": v(11.6, -12.64) * mm, "end": v(15.3, -16.11) * mm});
            skLineSegment(sketch, "E13.9.22.0", {"start": v(17.04, -14.26) * mm, "end": v(15.3, -16.11) * mm});
            skLineSegment(sketch, "E13.1.23.0", {"start": v(15.6, -7.13) * mm, "end": v(20.06, -9.58) * mm});
            skLineSegment(sketch, "E13.3.23.0", {"start": v(15.6, -7.13) * mm, "end": v(14.39, -9.36) * mm});
            skLineSegment(sketch, "E13.6.23.0", {"start": v(14.39, -9.36) * mm, "end": v(18.83, -11.8) * mm});
            skLineSegment(sketch, "E13.9.23.0", {"start": v(20.06, -9.58) * mm, "end": v(18.83, -11.8) * mm});
            skLineSegment(sketch, "E13.1.24.0", {"start": v(16.9, -3.03) * mm, "end": v(21.8, -4.29) * mm});
            skLineSegment(sketch, "E13.3.24.0", {"start": v(16.9, -3.03) * mm, "end": v(16.26, -5.48) * mm});
            skLineSegment(sketch, "E13.6.24.0", {"start": v(16.26, -5.48) * mm, "end": v(21.18, -6.75) * mm});
            skLineSegment(sketch, "E13.9.24.0", {"start": v(21.8, -4.29) * mm, "end": v(21.18, -6.75) * mm});
            skLineSegment(sketch, "E14.1.20.0", {"start": v(5.65, -21.5) * mm, "end": v(6.28, -23.44) * mm});
            skLineSegment(sketch, "E14.3.20.0", {"start": v(8.7, -22.66) * mm, "end": v(6.28, -23.44) * mm});
            skLineSegment(sketch, "E14.6.20.0", {"start": v(8.06, -20.71) * mm, "end": v(8.7, -22.66) * mm});
            skLineSegment(sketch, "E14.1.21.0", {"start": v(10.82, -19.41) * mm, "end": v(11.92, -21.14) * mm});
            skLineSegment(sketch, "E14.3.21.0", {"start": v(14.06, -19.78) * mm, "end": v(11.92, -21.14) * mm});
            skLineSegment(sketch, "E14.6.21.0", {"start": v(12.96, -18.05) * mm, "end": v(14.06, -19.78) * mm});
            skLineSegment(sketch, "E14.1.22.0", {"start": v(15.3, -16.11) * mm, "end": v(16.8, -17.51) * mm});
            skLineSegment(sketch, "E14.3.22.0", {"start": v(18.54, -15.66) * mm, "end": v(16.8, -17.51) * mm});
            skLineSegment(sketch, "E14.6.22.0", {"start": v(17.04, -14.26) * mm, "end": v(18.54, -15.66) * mm});
            skLineSegment(sketch, "E14.1.23.0", {"start": v(18.83, -11.8) * mm, "end": v(20.63, -12.79) * mm});
            skLineSegment(sketch, "E14.3.23.0", {"start": v(21.85, -10.56) * mm, "end": v(20.63, -12.79) * mm});
            skLineSegment(sketch, "E14.6.23.0", {"start": v(20.06, -9.58) * mm, "end": v(21.85, -10.56) * mm});
            skLineSegment(sketch, "E14.1.24.0", {"start": v(21.18, -6.75) * mm, "end": v(23.16, -7.26) * mm});
            skLineSegment(sketch, "E14.3.24.0", {"start": v(23.8, -4.8) * mm, "end": v(23.16, -7.26) * mm});
            skLineSegment(sketch, "E14.6.24.0", {"start": v(21.8, -4.29) * mm, "end": v(23.8, -4.8) * mm});
            skSolve(sketch);
        }
        {
            var Q0;
            Q0 = qSketchRegion(id + "F2", true);
            extrude(context, id + "F3", {"entities" : qUnion([Q0]), "operationType" : NewBodyOperationType.ADD, "depth" : 1.27 * mm, "hasSecondDirection" : true, "secondDirectionOppositeDirection" : true, "secondDirectionDepth" : 3.8 * mm});
        }
        {
            var Q0;
            Q0=qCreatedBy(makeId("Top.planeOp"),FACE);
            var sketch = newSketch(context, id + "F4", { "sketchPlane" : qUnion([Q0])});
            skLineSegment(sketch, "E15", {"start": v(-2.24, -21.76) * mm, "end": v(-2.24, -179.65) * mm});
            skLineSegment(sketch, "E16.MirrorCS", {"start": v(2.24, -21.76) * mm, "end": v(2.24, -179.65) * mm});
            skArc(sketch, "E17", {"start": v(-2.24, -179.65) * mm, "mid": v(0, -207.94) * mm, "end": v(2.24, -179.65) * mm});
            skCircle(sketch, "E18", {"center": v(0, -193.7) * mm, "radius": 9.15 * mm});
            skLineSegment(sketch, "E19", {"start": v(-2.24, -21.76) * mm, "end": v(2.24, -21.76) * mm});
            skSolve(sketch);
        }
        {
            var Q0;
            Q0 = qSketchRegion(id + "F4", true);
            extrude(context, id + "F5", {"entities" : qUnion([Q0]), "operationType" : NewBodyOperationType.ADD, "depth" : 3.8 * mm});
        }
    });
